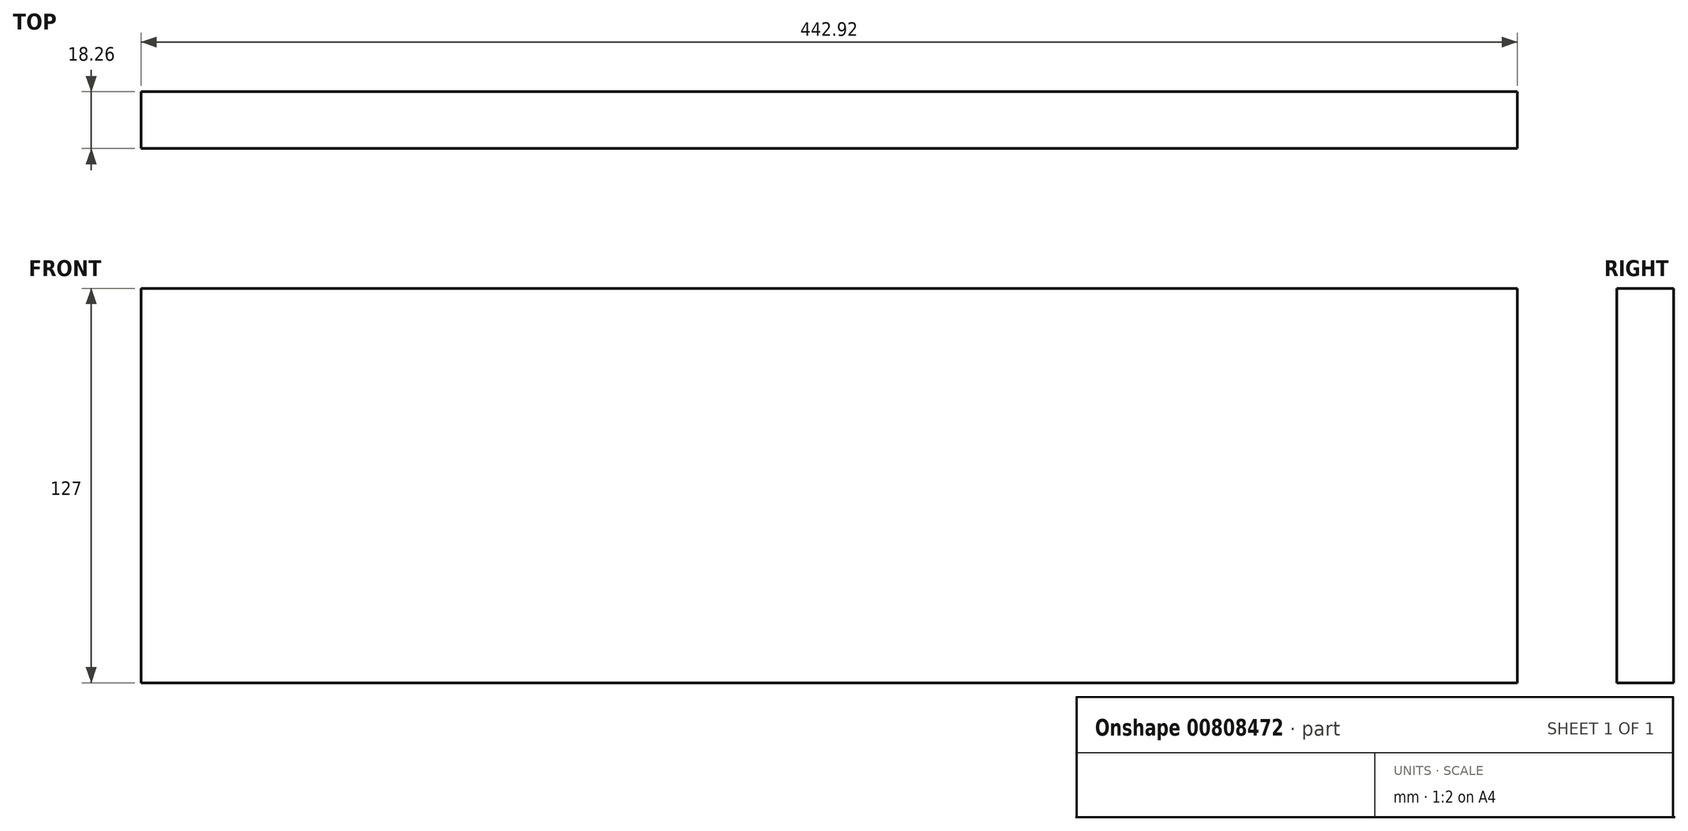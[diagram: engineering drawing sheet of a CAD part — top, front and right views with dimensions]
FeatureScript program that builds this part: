
annotation { "Feature Type Name" : "Feature", "Feature Type Description" : "" }
export const myFeature = defineFeature(function(context is Context, id is Id, definition is map)
    precondition{}
    {
        {
            var Q0;
            Q0=qCreatedBy(makeId("Front.planeOp"),FACE);
            var sketch = newSketch(context, id + "F0", { "sketchPlane" : qUnion([Q0])});
            skLineSegment(sketch, "E0.bottom", {"start": v(-221.46, 63.5) * mm, "end": v(221.46, 63.5) * mm});
            skLineSegment(sketch, "E0.top", {"start": v(-221.46, -63.5) * mm, "end": v(221.46, -63.5) * mm});
            skLineSegment(sketch, "E0.left", {"start": v(-221.46, 63.5) * mm, "end": v(-221.46, -63.5) * mm});
            skLineSegment(sketch, "E0.right", {"start": v(221.46, 63.5) * mm, "end": v(221.46, -63.5) * mm});
            skPoint(sketch, "E0.middle", {"position": v(0, 0) * mm});
            skSolve(sketch);
        }
        {
            var Q0;
            Q0 = qSketchRegion(id + "F0", true);
            extrude(context, id + "F1", {"entities" : qUnion([Q0]), "depth" : 18.26 * mm, "offsetDistance" : 25.4 * mm});
        }
    });
